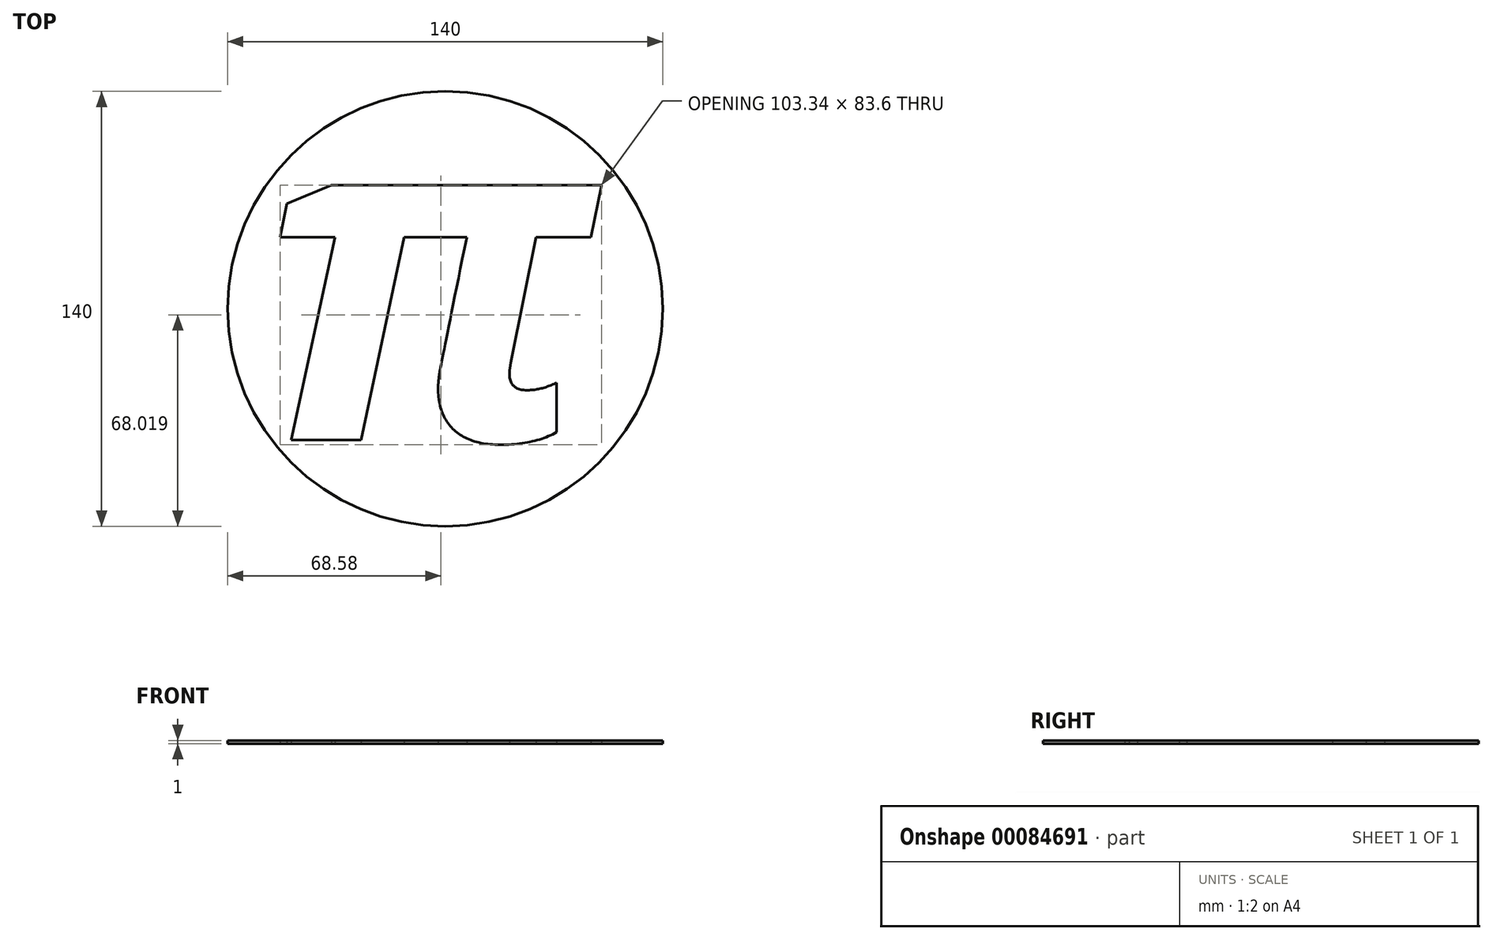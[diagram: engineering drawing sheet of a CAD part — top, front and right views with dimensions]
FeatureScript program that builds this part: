
annotation { "Feature Type Name" : "Feature", "Feature Type Description" : "" }
export const myFeature = defineFeature(function(context is Context, id is Id, definition is map)
    precondition{}
    {
        {
            var Q0;
            Q0=qCreatedBy(makeId("Top.planeOp"),FACE);
            var sketch = newSketch(context, id + "F0", { "sketchPlane" : qUnion([Q0])});
            skText(sketch, "E0", { "text": "π", "fontName": "OpenSans-BoldItalic.ttf"});
            skPoint(sketch, "E1", {"position": v(0, 0) * mm});
            skCircle(sketch, "E2", {"center": v(0, 0) * mm, "radius": 70 * mm});
            skLineSegment(sketch, "E3", {"start": v(0, 66) * mm, "end": v(0, 70) * mm, "construction": true});
            const initialGuessF0  = {"E0": [-0.06, -0.0423, 1, 0, 0.1083]};
            skSetInitialGuess(sketch, initialGuessF0);
            skSolve(sketch);
        }
        {
            var Q0;
            Q0=makeQuery(id+"F0.imprint","IMPRINT",FACE,{"disambiguationData":[TD([[makeQuery(id+"F0.imprint","IMPRINT",EDGE,{"derivedFrom":sQuery(id+"F0.wireOp",EDGE,"E0.sketch_text.stroke-0")}),1.0]])]});
            extrude(context, id + "F1", {"entities" : qUnion([Q0]), "depth" : 1 * mm});
        }
    });
